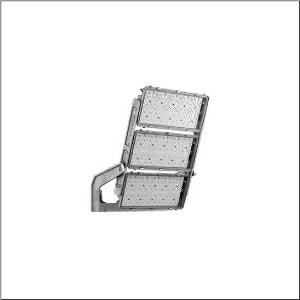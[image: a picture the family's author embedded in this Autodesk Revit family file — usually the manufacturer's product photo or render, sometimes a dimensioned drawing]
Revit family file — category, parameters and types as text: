
# Revit family: floodlight_fl_11_maxi_pro_remote___pl52_5xa779426d01ba_5366
name_source: partatom
category: Lighting Fixtures
units: mm (PartAtom-declared; Revit-internal decimal feet)

## family parameters
Cut with Voids When Loaded = No
Host = Face
Light Source = No
Part Type = Normal
Room Calculation Point = No
Round Connector Dimension = Use Diameter
Shared = No

## types (1)
- --- (1 x LED, 146220 lm, 1095.8 W, 4000K)
    Apparent Load = 1096 VA
    CIE Flux Codes = 24 55 98 100 100
    Color Rendering = 70
    Color Temperature = 4000K
    Default Elevation = 1800 mm
    Description = Floodlight FL 11  maxi  pro Remote floodlight; light control with lens of PMMA; cover panel of toughened safety glass, transparent; light distribution: PL52, asymmetric direct distribution, LEDcolour temperature: 4000K, rated luminous flux: 146.220lm, colour rendering: CRI > 70, light colour: 740; luminous efficacy: 133lm/W; brightness control: DALI 2 (1 DALI address); with terminal, 8-pole, max. 2.5mm², mains connection: 220..240V/380..400V AC, 50/60Hz, surge voltage resistance: line to ground: 10kV, ECG replaceable separately, LED unit replaceable without ESD environment, dustproof LED module, dimming range 10..100%, no afterglow with DALI off / DMX off command; 1096W floodlight with 3x LED unit of diecast aluminium, coated grey; length: 713mm / width: 651mm / height: 338mm; mounting bracket, of diecast aluminium, uncoated, natural, equipment: Longlife, protection rating (complete): IP66; insulation class (complete): insulation class I (protective earthing); certification: CE, ENEC, VDE; ball protection: ball impact resistance with accessories, rated ambient temperature 10°C, only for outdoor installations, permissible operating ambient temperature: -40..+40°C, permissible storage temperature: -40..+85°C; packaging unit: 1 piece

Light Distribution: PL52
    Height = 320 mm
    Lamp = 1 x LED
    Lamp Light Flux = 146220 lm
    Lamp Power = 1095.8 W
    Lamp count = 1
    Length = 1002 mm
    Luminous efficacy = 133 lm/W
    Manufacturer = Siteco
    ModVariant = No
    Model = 5XA779426D01BA
    Number of Poles = 1
    OnlyDefault = Yes
    Power Factor = 1
    Product Name = Floodlight FL 11 maxi pro Remote | PL52
    Product group = floodlight | pylon top
    ProductGroupID = 6101
    Protection Class = Protection class I
    Protection Degree = IP 66
    RLX_Detail_Level = 1
    RlxData = <blob elided: 52605 chars, md5=4089bdc3>
    Socket = socket
    Standby Power = 0 W
    System Light Flux = 146220 lm
    System Power = 1096 W
    Type Comments = factory setting: luminous flux: 100 % | dim-lin: 254 | 760 mA
    Type Image = l_1006784.jpg
    URL = http://relux.com
    VarID = @adj_007421
    Voltage = 0 V
    Weight = 0.00 kg
    Width = 655 mm

## geometry (parser evidence)
native form markers: Blend x4, Sweep x15
no freeform markers — native parametric forms only
